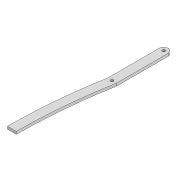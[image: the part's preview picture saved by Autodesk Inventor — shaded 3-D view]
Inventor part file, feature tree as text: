
AUTODESK INVENTOR PART (.ipt)
format: ipt  version: 2022 (Build 260153000, 153)  size: 113,152 bytes
history: native  units: mm
features: extrude x2, sketch x2
ambient origin geometry x8: Origin, YZ Plane, XZ Plane, XY Plane, X Axis, Y Axis, Z Axis, Center Point
bodies: Solid1 (feature_tree)
feature tree (4):
  extrude  "Extrusion1"  Depth=3.3mm
  extrude  "Extrusion2"  Depth=312.648mm
  sketch  "Sketch1"  dims[d0=3.3mm d1=3.3mm]
  sketch  "Sketch2"  dims[d2=10.0mm d3=312.648mm d6=3.0mm d7=0.0mm d10=3.3mm d11=42.6mm d12=3.3mm d13=254.274mm d16=600.0mm d17=600.0mm d18=10.0mm d19=0.0mm]
